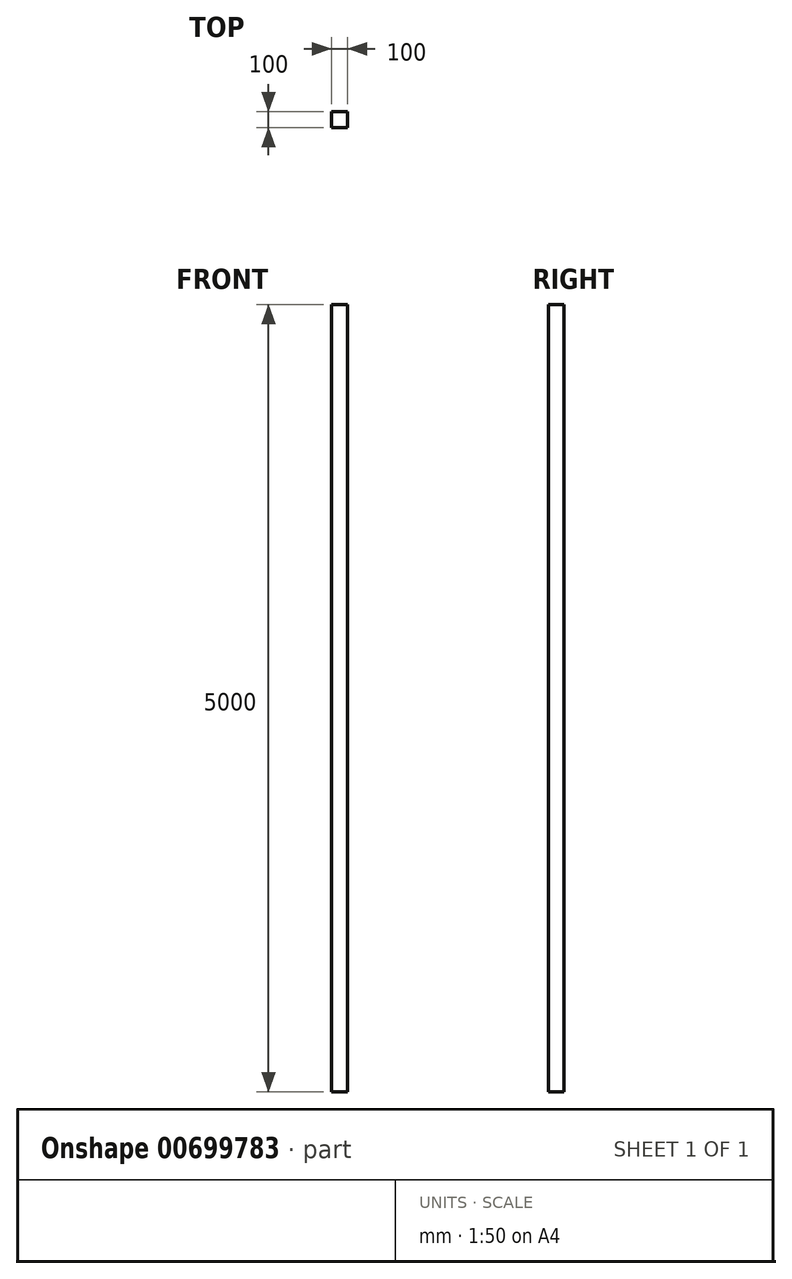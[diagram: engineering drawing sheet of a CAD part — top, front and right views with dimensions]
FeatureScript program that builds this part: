
annotation { "Feature Type Name" : "Feature", "Feature Type Description" : "" }
export const myFeature = defineFeature(function(context is Context, id is Id, definition is map)
    precondition{}
    {
        {
            var Q0;
            Q0=qCreatedBy(makeId("Top.planeOp"),FACE);
            var sketch = newSketch(context, id + "F0", { "sketchPlane" : qUnion([Q0])});
            skLineSegment(sketch, "E0.bottom", {"start": v(142.56, -55.83) * mm, "end": v(242.56, -55.83) * mm});
            skLineSegment(sketch, "E0.top", {"start": v(142.56, -155.83) * mm, "end": v(242.56, -155.83) * mm});
            skLineSegment(sketch, "E0.left", {"start": v(142.56, -55.83) * mm, "end": v(142.56, -155.83) * mm});
            skLineSegment(sketch, "E0.right", {"start": v(242.56, -55.83) * mm, "end": v(242.56, -155.83) * mm});
            skSolve(sketch);
        }
        {
            var Q0;
            Q0=qSketchRegion(id+"F0",true);
            extrude(context, id + "F1", {"entities" : qUnion([Q0]), "depth" : 5000 * mm, "offsetDistance" : 25 * mm});
        }
    });
